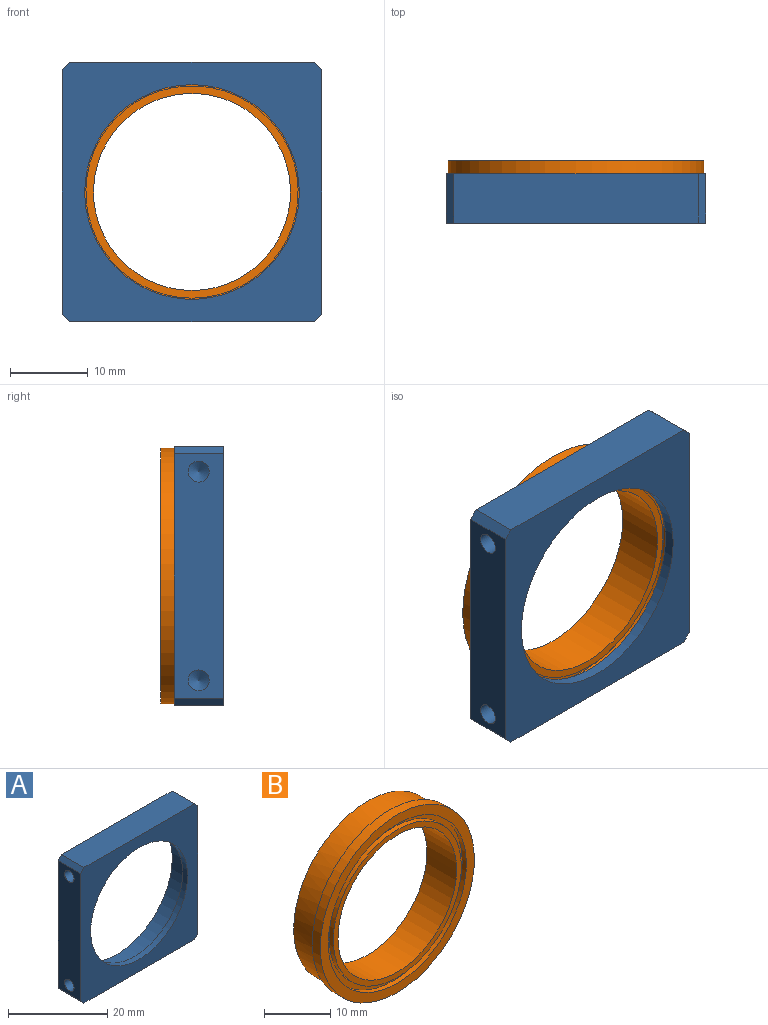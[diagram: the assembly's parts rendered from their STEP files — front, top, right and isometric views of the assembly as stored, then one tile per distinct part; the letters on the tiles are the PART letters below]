
ASSEMBLY  parts=2 mates=1
PART A: 21 faces, bbox 33.5x6.4x33.5 mm
  f0: cylinder r=1.35mm len=5.08mm, axis (1,0,0), area 43.2mm2, adj f1,f10
  f1: cone r=1.35mm half-angle=59deg, axis (1,0,0), area 6.7mm2, adj f0
  f2: cylinder r=1.35mm len=5.08mm, axis (1,0,0), area 43.2mm2, adj f3,f10
  f3: cone r=1.35mm half-angle=59deg, axis (1,0,0), area 6.7mm2, adj f2
  f4: cylinder r=1.35mm len=5.08mm, axis (-1,0,0), area 43.2mm2, adj f5,f12
  f5: cone r=1.35mm half-angle=59deg, axis (-1,0,0), area 6.7mm2, adj f4
  f6: cylinder r=1.35mm len=5.08mm, axis (-1,0,0), area 43.2mm2, adj f7,f12
  f7: cone r=1.35mm half-angle=59deg, axis (-1,0,0), area 6.7mm2, adj f6
  f8: cylinder r=13.84mm len=27.69mm, axis (0,1,0), area 121.5mm2, adj f15,f16
  f9: cylinder r=15.81mm len=31.62mm, axis (0,1,0), area 492.1mm2, adj f14,f16
  f10: plane 31.5x6.35mm, normal (1,0,0), area 188.5mm2, adj f0,f2,f14,f15,f18,f19
  f11: plane 31.5x6.35mm, normal (0,0,-1), area 200mm2, adj f14,f15,f17,f18
  f12: plane 31.5x6.35mm, normal (-1,0,0), area 188.5mm2, adj f4,f6,f14,f15,f17,f20
  f13: plane 31.5x6.35mm, normal (0,0,1), area 200mm2, adj f14,f15,f19,f20
  f14: plane 33.53x33.53mm, normal (0,1,0), area 336.7mm2, adj f9,f10,f11,f12,f13,f17,f18,f19
  f15: plane 33.53x33.53mm, normal (0,-1,0), area 520mm2, adj f8,f10,f11,f12,f13,f17,f18,f19
  f16: plane 31.62x31.62mm, normal (0,1,0), area 183.4mm2, adj f8,f9
  f17: plane 6.35x1.02mm, normal (-0.71,0,-0.71), area 9.1mm2, adj f11,f12,f14,f15
  f18: plane 6.35x1.02mm, normal (0.71,0,-0.71), area 9.1mm2, adj f10,f11,f14,f15
  f19: plane 6.35x1.02mm, normal (0.71,0,0.71), area 9.1mm2, adj f10,f13,f14,f15
  f20: plane 6.35x1.02mm, normal (-0.71,0,0.71), area 9.1mm2, adj f12,f13,f14,f15
PART B: 14 faces, bbox 33x6.4x33 mm
  f0: cylinder r=16.48mm len=32.96mm, axis (0,-1,0), area 177.5mm2, adj f10,f13
  f1: cylinder r=13.69mm len=27.38mm, axis (0,-1,0), area 76.5mm2, adj f7,f12
  f2: cylinder r=14.76mm len=29.52mm, axis (0,-1,0), area 82.4mm2, adj f10,f12
  f3: cylinder r=13.69mm len=27.38mm, axis (0,1,0), area 76.5mm2, adj f8,f11
  f4: cylinder r=14.76mm len=29.52mm, axis (0,1,0), area 82.4mm2, adj f9,f11
  f5: cylinder r=12.7mm len=25.4mm, axis (0,-1,0), area 506.7mm2, adj f7,f8
  f6: cylinder r=15.81mm len=31.62mm, axis (0,-1,0), area 460.5mm2, adj f9,f13
  f7: plane 27.38x27.38mm, normal (0,-1,0), area 82.1mm2, adj f1,f5
  f8: plane 27.38x27.38mm, normal (0,1,0), area 82.1mm2, adj f3,f5
  f9: plane 31.62x31.62mm, normal (0,1,0), area 101.2mm2, adj f4,f6
  f10: plane 32.96x32.96mm, normal (0,-1,0), area 168.9mm2, adj f0,f2
  f11: plane 29.52x29.52mm, normal (0,1,0), area 95.3mm2, adj f3,f4
  f12: plane 29.52x29.52mm, normal (0,-1,0), area 95.3mm2, adj f1,f2
  f13: plane 32.96x32.96mm, normal (0,1,0), area 67.6mm2, adj f0,f6
PLACE A t=(8.08,10.2,30.88)mm
PLACE B rot(axis=(1,0,0),180deg) t=(8.08,18.27,30.88)mm
MATE fastened B.f0 <-> A.f8  axis (0,-1,0) through (8.08,11.92,30.88)mm
